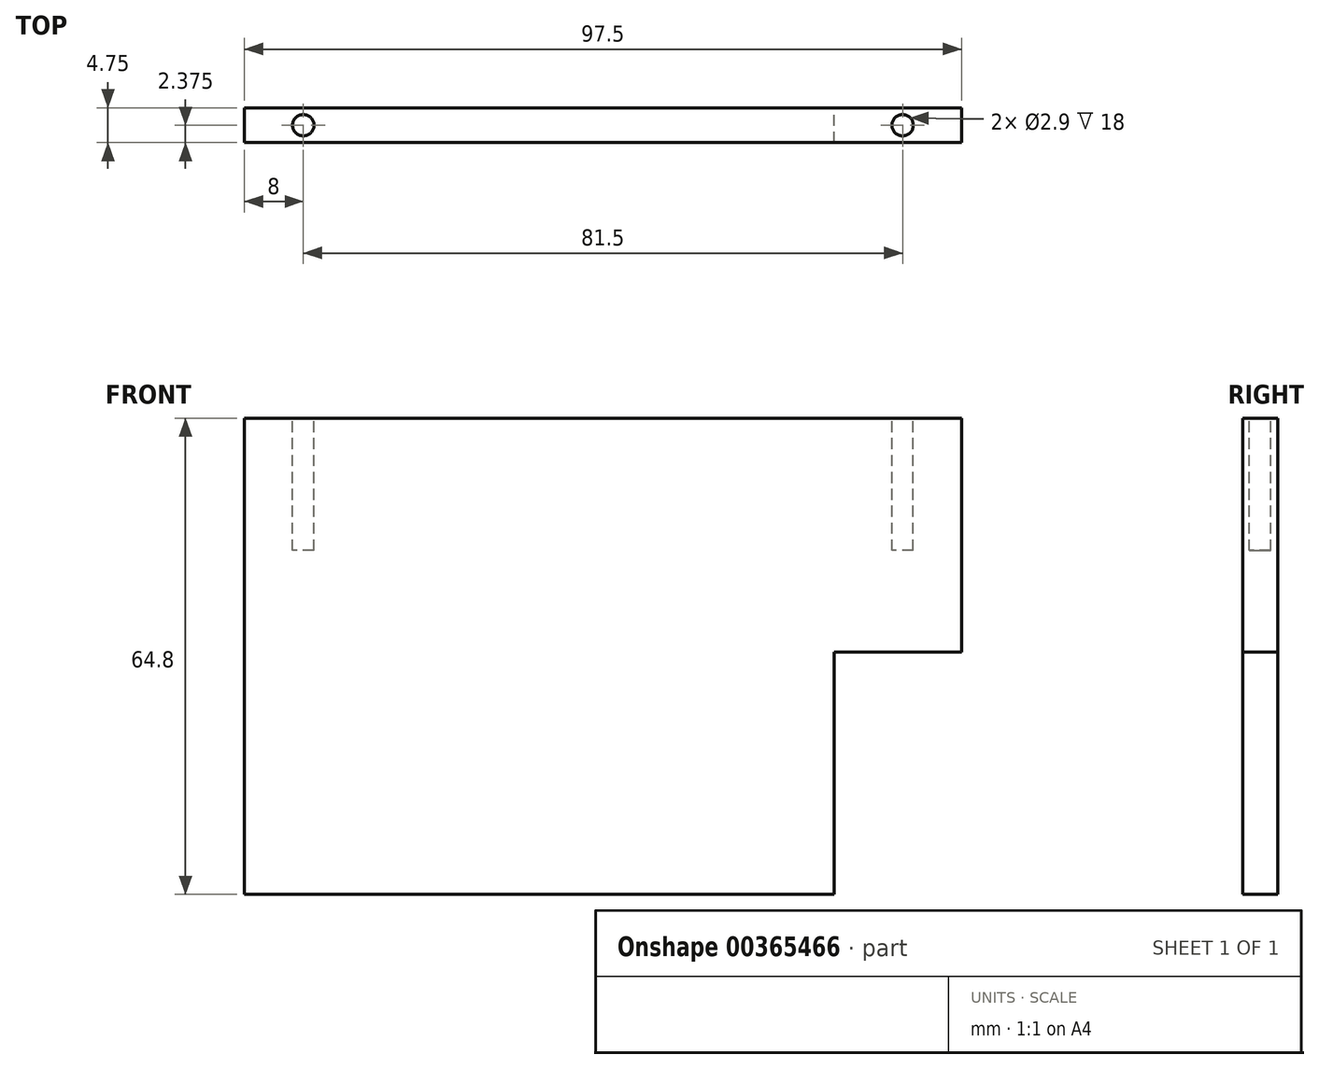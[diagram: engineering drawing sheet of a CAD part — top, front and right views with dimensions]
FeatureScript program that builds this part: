
annotation { "Feature Type Name" : "Feature", "Feature Type Description" : "" }
export const myFeature = defineFeature(function(context is Context, id is Id, definition is map)
    precondition{}
    {
        {
            var Q0;
            Q0=qCreatedBy(makeId("Front.planeOp"),FACE);
            var sketch = newSketch(context, id + "F0", { "sketchPlane" : qUnion([Q0])});
            skLineSegment(sketch, "E0.bottom", {"start": v(0, 0) * mm, "end": v(97.5, 0) * mm});
            skLineSegment(sketch, "E0.top", {"start": v(0, 64.8) * mm, "end": v(97.5, 64.8) * mm});
            skLineSegment(sketch, "E0.left", {"start": v(0, 0) * mm, "end": v(0, 64.8) * mm});
            skLineSegment(sketch, "E0.right", {"start": v(97.5, 33) * mm, "end": v(97.5, 64.8) * mm});
            skLineSegment(sketch, "E1.top", {"start": v(97.5, 33) * mm, "end": v(80.2, 33) * mm});
            skLineSegment(sketch, "E1.right", {"start": v(80.2, 0) * mm, "end": v(80.2, 33) * mm});
            skSolve(sketch);
        }
        {
            var Q0;
            Q0 = qSketchRegion(id + "F0", true);
            extrude(context, id + "F1", {"entities" : qUnion([Q0]), "depth" : 4.75 * mm});
        }
        {
            var Q0;
            Q0=makeQuery(id+"F1.opExtrude","SWEPT_FACE",FACE,{"disambiguationData":[OSD([sQuery(id+"F0.wireOp",EDGE,"E0.top")])]});
            var sketch = newSketch(context, id + "F2", { "sketchPlane" : qUnion([Q0])});
            skLineSegment(sketch, "E2", {"start": v(97.5, -2.38) * mm, "end": v(89.5, -2.38) * mm});
            skLineSegment(sketch, "E3", {"start": v(0, -2.38) * mm, "end": v(8, -2.38) * mm});
            skCircle(sketch, "E4", {"center": v(89.5, -2.38) * mm, "radius": 1.45 * mm});
            skCircle(sketch, "E5", {"center": v(8, -2.38) * mm, "radius": 1.45 * mm});
            skSolve(sketch);
        }
        {
            var Q0;
            Q0 = qSketchRegion(id + "F2", true);
            extrude(context, id + "F3", {"entities" : qUnion([Q0]), "operationType" : NewBodyOperationType.REMOVE, "oppositeDirection" : true, "depth" : 18 * mm});
        }
    });
